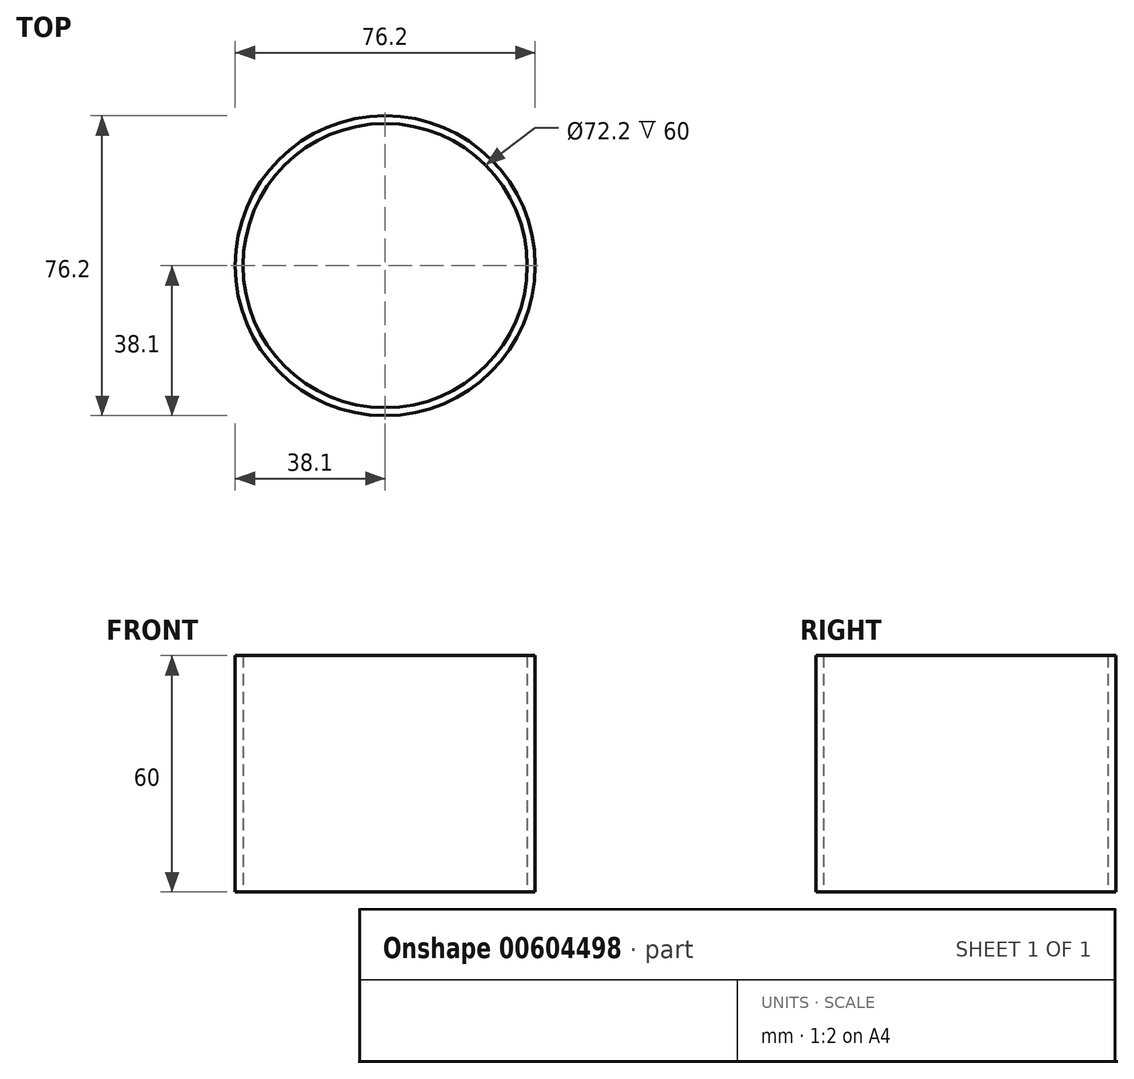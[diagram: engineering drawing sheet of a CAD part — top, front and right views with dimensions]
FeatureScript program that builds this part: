
annotation { "Feature Type Name" : "Feature", "Feature Type Description" : "" }
export const myFeature = defineFeature(function(context is Context, id is Id, definition is map)
    precondition{}
    {
        {
            var Q0;
            Q0=qCreatedBy(makeId("Top.planeOp"),FACE);
            var sketch = newSketch(context, id + "F0", { "sketchPlane" : qUnion([Q0])});
            skCircle(sketch, "E0", {"center": v(0, 0) * mm, "radius": 38.1 * mm});
            skCircle(sketch, "E1.0", {"center": v(0, 0) * mm, "radius": 36.1 * mm});
            skSolve(sketch);
        }
        {
            var Q0;
            Q0=makeQuery(id+"F0.imprint","IMPRINT",FACE,{"disambiguationData":[TD([[makeQuery(id+"F0.imprint","IMPRINT",EDGE,{"derivedFrom":sQuery(id+"F0.wireOp",EDGE,"E0")}),1.0]])]});
            extrude(context, id + "F1", {"entities" : qUnion([Q0]), "depth" : 60 * mm, "offsetDistance" : 25 * mm});
        }
        {
            var Q0;
            Q0=qCreatedBy(makeId("Right.planeOp"),FACE);
            var sketch = newSketch(context, id + "F2", { "sketchPlane" : qUnion([Q0])});
            skLineSegment(sketch, "E2.0", {"start": v(-38.1, 60) * mm, "end": v(-35.97, 60) * mm});
            skLineSegment(sketch, "E3", {"start": v(-38.1, 60) * mm, "end": v(-19.05, 111.45) * mm});
            skLineSegment(sketch, "E4", {"start": v(0, 60) * mm, "end": v(0, 152.03) * mm, "construction": true});
            skPoint(sketch, "E4.startSnap0", {"position": v(0, 60) * mm});
            skLineSegment(sketch, "E5", {"start": v(-19.05, 111.45) * mm, "end": v(-19.05, 152.03) * mm});
            skLineSegment(sketch, "E6", {"start": v(-19.05, 152.03) * mm, "end": v(-17.05, 152.03) * mm});
            skPoint(sketch, "E7.end.orphan", {"position": v(0, 111.46) * mm});
            skPoint(sketch, "E8.orphan", {"position": v(38.1, 60) * mm});
            skLineSegment(sketch, "E9.0", {"start": v(-17.05, 111.09) * mm, "end": v(-17.05, 152.03) * mm});
            skLineSegment(sketch, "E9.1", {"start": v(-35.97, 60) * mm, "end": v(-17.05, 111.09) * mm});
            skSolve(sketch);
        }
        {
            var Q0;
            Q0=sQuery(id+"F2.wireOp",EDGE,"E4");
            var Q1;
            Q1=sQuery(id+"F2.wireOp",EDGE,"E5");
            var Q2;
            Q2=sQuery(id+"F2.wireOp",EDGE,"E3");
            var Q3;
            Q3=sQuery(id+"F2.wireOp",EDGE,"E6");
            var Q4;
            Q4=sQuery(id+"F2.wireOp",EDGE,"E9.0");
            var Q5;
            Q5=sQuery(id+"F2.wireOp",EDGE,"E9.1");
            var Q6;
            Q6=sQuery(id+"F2.wireOp",EDGE,"E2.0");
            var Q7;
            Q7=sQuery(id+"F2.wireOp",EDGE,"E4");
            revolve(context, id + "F3", {"bodyType" : ToolBodyType.SURFACE, "surfaceEntities" : qUnion([Q0, Q1, Q2, Q3, Q4, Q5, Q6]), "axis" : qUnion([Q7]), "revolveType" : RevolveType.FULL});
        }
    });
